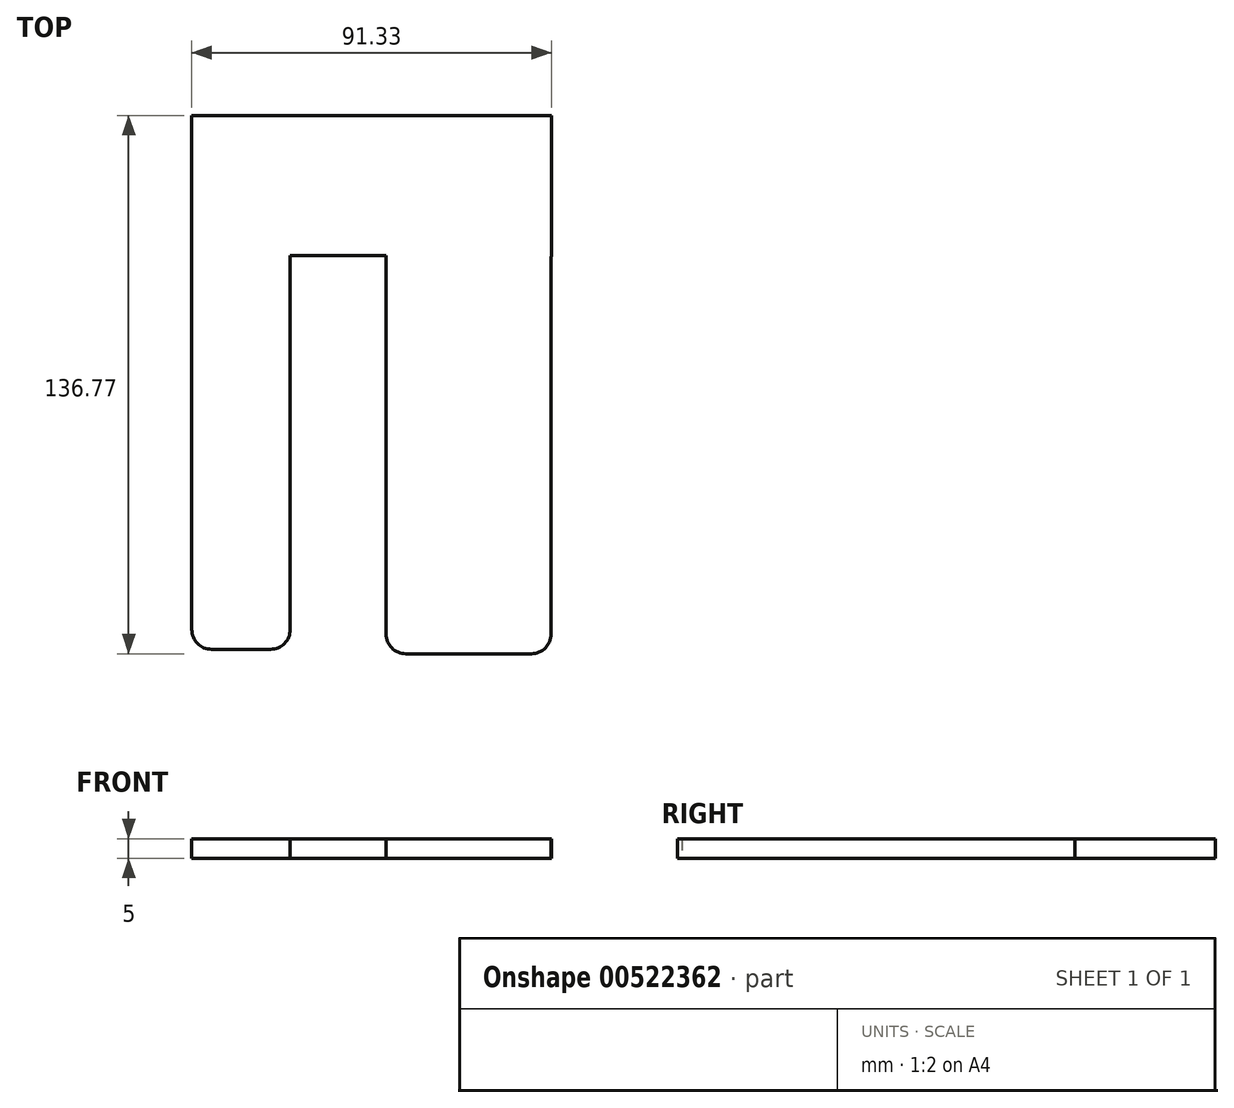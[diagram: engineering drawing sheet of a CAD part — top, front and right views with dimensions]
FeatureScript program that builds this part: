
annotation { "Feature Type Name" : "Feature", "Feature Type Description" : "" }
export const myFeature = defineFeature(function(context is Context, id is Id, definition is map)
    precondition{}
    {
        {
            var Q0;
            Q0=qCreatedBy(makeId("Top.planeOp"),FACE);
            var sketch = newSketch(context, id + "F0", { "sketchPlane" : qUnion([Q0])});
            skLineSegment(sketch, "E0.bottom", {"start": v(-26.87, 42.78) * mm, "end": v(-68.2, 42.78) * mm});
            skLineSegment(sketch, "E0.top", {"start": v(-26.87, 6.99) * mm, "end": v(-68.2, 6.99) * mm});
            skLineSegment(sketch, "E0.left", {"start": v(-26.87, 42.78) * mm, "end": v(-26.87, 6.99) * mm});
            skLineSegment(sketch, "E0.right", {"start": v(-68.2, 42.78) * mm, "end": v(-68.2, 6.99) * mm});
            skSolve(sketch);
        }
        {
            var Q0;
            Q0=makeQuery(id+"F0.imprint","IMPRINT",FACE,{"disambiguationData":[TD([[makeQuery(id+"F0.imprint","IMPRINT",EDGE,{"derivedFrom":sQuery(id+"F0.wireOp",EDGE,"E0.bottom")}),1.0]])]});
            extrude(context, id + "F1", {"entities" : qUnion([Q0]), "depth" : 5 * mm, "offsetDistance" : 25 * mm});
        }
        {
            var Q0;
            Q0=qCreatedBy(makeId("Top.planeOp"),FACE);
            var sketch = newSketch(context, id + "F2", { "sketchPlane" : qUnion([Q0])});
            skLineSegment(sketch, "E1.bottom", {"start": v(-26.94, 7.15) * mm, "end": v(-68.84, 7.15) * mm});
            skLineSegment(sketch, "E1.top", {"start": v(-26.94, -93.99) * mm, "end": v(-68.84, -93.99) * mm});
            skLineSegment(sketch, "E1.left", {"start": v(-26.94, 7.15) * mm, "end": v(-26.94, -93.99) * mm});
            skLineSegment(sketch, "E1.right", {"start": v(-68.84, 7.15) * mm, "end": v(-68.84, -93.99) * mm});
            skSolve(sketch);
        }
        {
            var Q0;
            Q0=makeQuery(id+"F2.imprint","IMPRINT",FACE,{"disambiguationData":[TD([[makeQuery(id+"F2.imprint","IMPRINT",EDGE,{"derivedFrom":sQuery(id+"F2.wireOp",EDGE,"E1.bottom")}),1.0]])]});
            extrude(context, id + "F3", {"entities" : qUnion([Q0]), "operationType" : NewBodyOperationType.ADD, "depth" : 5 * mm, "offsetDistance" : 25 * mm});
        }
        {
            var Q0;
            Q0=makeQuery(id+"F1.opExtrude","SWEPT_FACE",FACE,{"disambiguationData":[OSD([sQuery(id+"F0.wireOp",EDGE,"E0.right")])]});
            extrude(context, id + "F4", {"entities" : qUnion([Q0]), "operationType" : NewBodyOperationType.ADD, "depth" : 25 * mm, "offsetDistance" : 25 * mm});
        }
        {
            var Q0;
            Q0=makeQuery(id+"F4.opExtrude","CAP_FACE",FACE,{"disambiguationData":[OSD([sQuery(id+"F0.wireOp",EDGE,"E0.right")])],"isStart":false});
            extrude(context, id + "F5", {"entities" : qUnion([Q0]), "operationType" : NewBodyOperationType.ADD, "depth" : 25 * mm, "offsetDistance" : 25 * mm});
        }
        {
            var Q0;
            Q0=qCreatedBy(makeId("Top.planeOp"),FACE);
            var sketch = newSketch(context, id + "F6", { "sketchPlane" : qUnion([Q0])});
            skLineSegment(sketch, "E2.bottom", {"start": v(-118.2, 7.15) * mm, "end": v(-93.2, 7.15) * mm});
            skLineSegment(sketch, "E2.top", {"start": v(-118.2, -92.85) * mm, "end": v(-93.2, -92.85) * mm});
            skLineSegment(sketch, "E2.left", {"start": v(-118.2, 7.15) * mm, "end": v(-118.2, -92.85) * mm});
            skLineSegment(sketch, "E2.right", {"start": v(-93.2, 7.15) * mm, "end": v(-93.2, -92.85) * mm});
            skSolve(sketch);
        }
        {
            var Q0;
            Q0=makeQuery(id+"F6.imprint","IMPRINT",FACE,{"disambiguationData":[TD([[makeQuery(id+"F6.imprint","IMPRINT",EDGE,{"derivedFrom":sQuery(id+"F6.wireOp",EDGE,"E2.bottom")}),-1.0]])]});
            extrude(context, id + "F7", {"entities" : qUnion([Q0]), "operationType" : NewBodyOperationType.ADD, "depth" : 5 * mm, "offsetDistance" : 25 * mm});
        }
        {
            var Q0;
            Q0=makeQuery(id+"F7.opExtrude","SWEPT_EDGE",EDGE,{"disambiguationData":[OSD([sQuery(id+"F6.wireOp",EDGE,"E2.top"),sQuery(id+"F6.wireOp",EDGE,"E2.left")])]});
            var Q1;
            Q1=makeQuery(id+"F7.opExtrude","SWEPT_EDGE",EDGE,{"disambiguationData":[OSD([sQuery(id+"F6.wireOp",EDGE,"E2.top"),sQuery(id+"F6.wireOp",EDGE,"E2.right")])]});
            var Q2;
            Q2=makeQuery(id+"F3.opExtrude","SWEPT_EDGE",EDGE,{"disambiguationData":[OSD([sQuery(id+"F2.wireOp",EDGE,"E1.top"),sQuery(id+"F2.wireOp",EDGE,"E1.right")])]});
            var Q3;
            Q3=makeQuery(id+"F3.opExtrude","SWEPT_EDGE",EDGE,{"disambiguationData":[OSD([sQuery(id+"F2.wireOp",EDGE,"E1.top"),sQuery(id+"F2.wireOp",EDGE,"E1.left")])]});
            fillet(context, id + "F8", {"entities" : qUnion([Q0, Q1, Q2, Q3]), "radius" : 5 * mm, "tangentPropagation" : true, "allowEdgeOverflow" : false});
        }
    });
